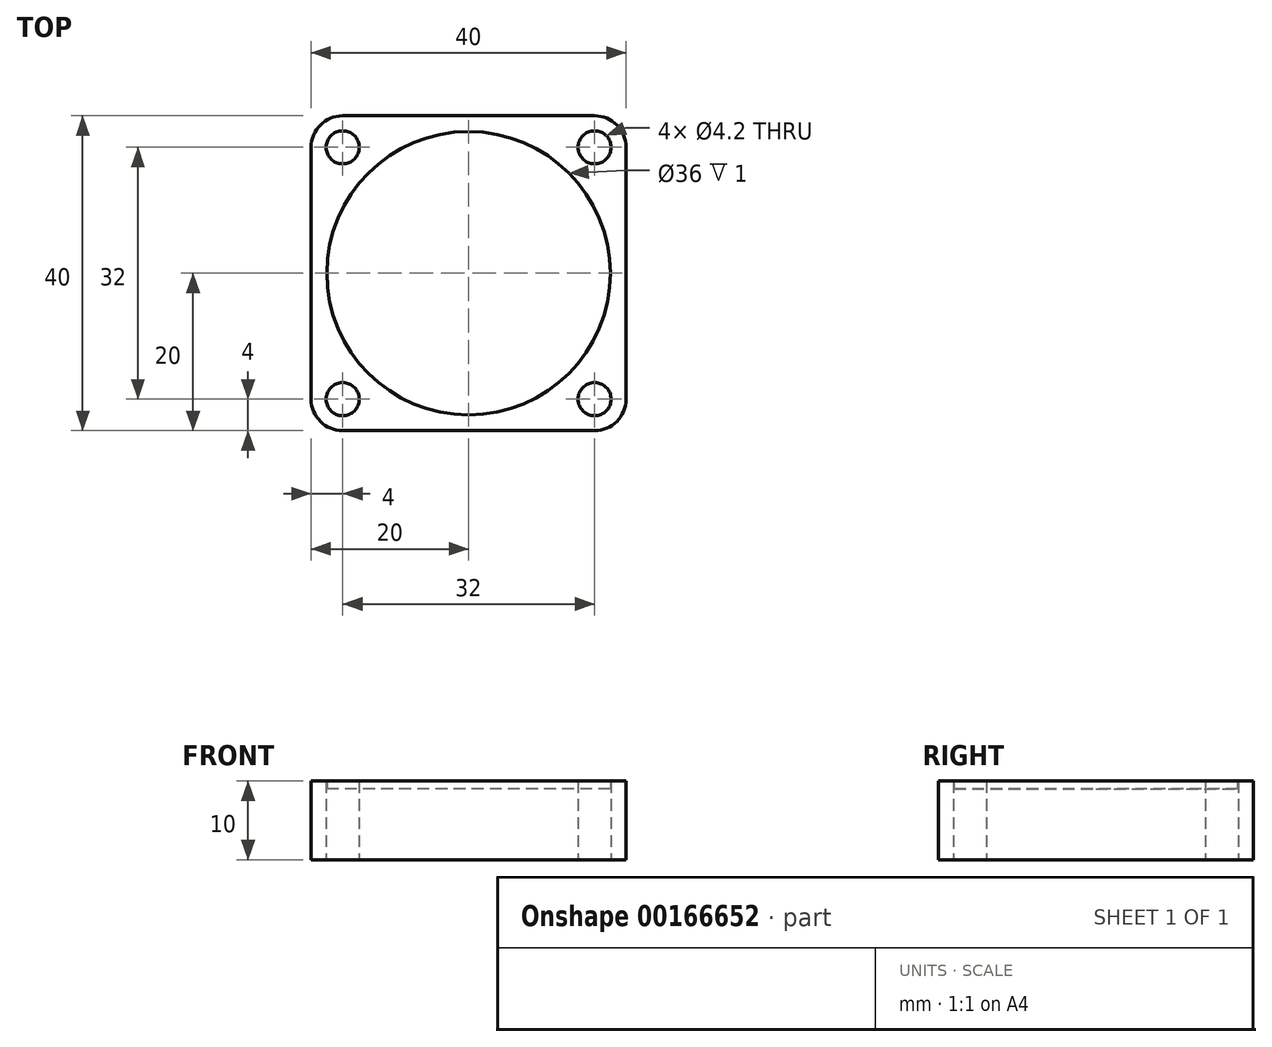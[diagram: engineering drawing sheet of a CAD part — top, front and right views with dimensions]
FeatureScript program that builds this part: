
annotation { "Feature Type Name" : "Feature", "Feature Type Description" : "" }
export const myFeature = defineFeature(function(context is Context, id is Id, definition is map)
    precondition{}
    {
        {
            var Q0;
            Q0=qCreatedBy(makeId("Top.planeOp"),FACE);
            var sketch = newSketch(context, id + "F0", { "sketchPlane" : qUnion([Q0])});
            skLineSegment(sketch, "E0.bottom", {"start": v(20, -20) * mm, "end": v(-20, -20) * mm});
            skLineSegment(sketch, "E0.top", {"start": v(20, 20) * mm, "end": v(-20, 20) * mm});
            skLineSegment(sketch, "E0.left", {"start": v(20, -20) * mm, "end": v(20, 20) * mm});
            skLineSegment(sketch, "E0.right", {"start": v(-20, -20) * mm, "end": v(-20, 20) * mm});
            skPoint(sketch, "E0.middle", {"position": v(0, 0) * mm});
            skCircle(sketch, "E1", {"center": v(0, 0) * mm, "radius": 18 * mm});
            skLineSegment(sketch, "E2.bottom", {"start": v(16, -16) * mm, "end": v(-16, -16) * mm, "construction": true});
            skLineSegment(sketch, "E2.top", {"start": v(16, 16) * mm, "end": v(-16, 16) * mm, "construction": true});
            skLineSegment(sketch, "E2.left", {"start": v(16, -16) * mm, "end": v(16, 16) * mm, "construction": true});
            skLineSegment(sketch, "E2.right", {"start": v(-16, -16) * mm, "end": v(-16, 16) * mm, "construction": true});
            skSolve(sketch);
        }
        {
            var Q0;
            Q0 = qSketchRegion(id + "F0", true);
            extrude(context, id + "F1", {"entities" : qUnion([Q0]), "depth" : 10 * mm});
        }
        {
            var Q0;
            Q0=makeQuery(id+"F0.imprint","IMPRINT",FACE,{"disambiguationData":[TD([[makeQuery(id+"F0.imprint","IMPRINT",EDGE,{"derivedFrom":sQuery(id+"F0.wireOp",EDGE,"E1")}),1.0]])]});
            extrude(context, id + "F2", {"entities" : qUnion([Q0]), "operationType" : NewBodyOperationType.ADD, "depth" : 9 * mm});
        }
        {
            var Q0;
            Q0=sQuery(id+"F0.wireOp",VERTEX,"E2.right.end");
            var Q1;
            Q1=sQuery(id+"F0.wireOp",VERTEX,"E2.right.start");
            var Q2;
            Q2=sQuery(id+"F0.wireOp",VERTEX,"E2.left.start");
            var Q3;
            Q3=sQuery(id+"F0.wireOp",VERTEX,"E2.left.end");
            var Q4;
            Q4=makeQuery(id+"F1.opExtrude","SWEPT_BODY",BODY,{"disambiguationData":[OSD([sQuery(id+"F0.wireOp",EDGE,"E0.bottom"),sQuery(id+"F0.wireOp",EDGE,"E0.top"),sQuery(id+"F0.wireOp",EDGE,"E0.left"),sQuery(id+"F0.wireOp",EDGE,"E0.right"),sQuery(id+"F0.wireOp",EDGE,"E1")])]});
            hole(context, id + "F3", {"style" : HoleStyle.SIMPLE, "endStyle" : HoleEndStyle.THROUGH, "oppositeDirection" : true, "holeDiameter" : 4.2 * mm, "locations" : qUnion([Q0, Q1, Q2, Q3]), "scope" : qUnion([Q4]), "isTappedThrough" : true});
        }
        {
            var Q0;
            Q0=makeQuery(id+"F1.opExtrude","SWEPT_EDGE",EDGE,{"disambiguationData":[OSD([sQuery(id+"F0.wireOp",EDGE,"E0.bottom"),sQuery(id+"F0.wireOp",EDGE,"E0.right")])]});
            var Q1;
            Q1=makeQuery(id+"F1.opExtrude","SWEPT_EDGE",EDGE,{"disambiguationData":[OSD([sQuery(id+"F0.wireOp",EDGE,"E0.top"),sQuery(id+"F0.wireOp",EDGE,"E0.right")])]});
            var Q2;
            Q2=makeQuery(id+"F1.opExtrude","SWEPT_EDGE",EDGE,{"disambiguationData":[OSD([sQuery(id+"F0.wireOp",EDGE,"E0.top"),sQuery(id+"F0.wireOp",EDGE,"E0.left")])]});
            var Q3;
            Q3=makeQuery(id+"F1.opExtrude","SWEPT_EDGE",EDGE,{"disambiguationData":[OSD([sQuery(id+"F0.wireOp",EDGE,"E0.bottom"),sQuery(id+"F0.wireOp",EDGE,"E0.left")])]});
            fillet(context, id + "F4", {"entities" : qUnion([Q0, Q1, Q2, Q3]), "radius" : 4 * mm, "tangentPropagation" : true, "allowEdgeOverflow" : false});
        }
    });
